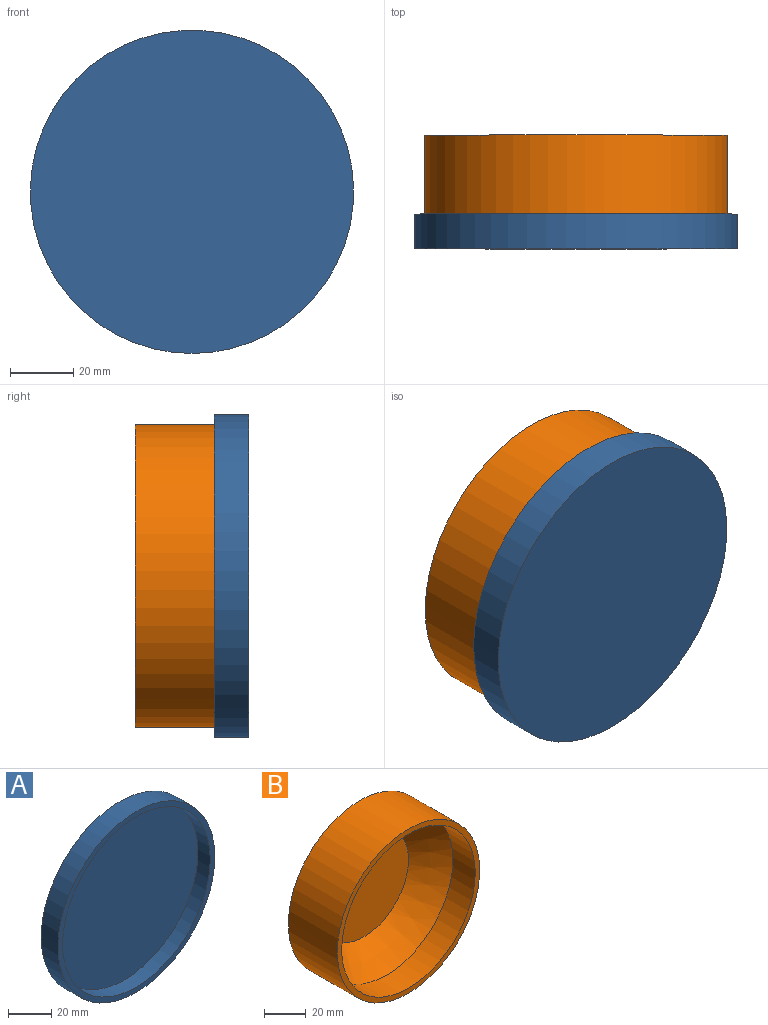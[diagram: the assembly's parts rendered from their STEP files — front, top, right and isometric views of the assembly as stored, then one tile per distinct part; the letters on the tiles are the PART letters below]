
ASSEMBLY  parts=2 mates=1
PART A: 5 faces, bbox 102.5x11x102.5 mm
  f0: cylinder r=48.25mm len=96.5mm, axis (0,1,0), area 2425.3mm2, adj f2,f3
  f1: cylinder r=51.25mm len=102.5mm, axis (0,1,0), area 3542.1mm2, adj f2,f4
  f2: plane 102.5x102.5mm, normal (0,-1,0), area 937.8mm2, adj f0,f1
  f3: plane 96.5x96.5mm, normal (0,-1,0), area 7313.8mm2, adj f0
  f4: plane 102.5x102.5mm, normal (0,1,0), area 8251.6mm2, adj f1
PART B: 6 faces, bbox 96x33x96 mm
  f0: cylinder r=45mm len=90mm, axis (0,1,0), area 4241.2mm2, adj f2,f5
  f1: cylinder r=48mm len=96mm, axis (0,1,0), area 9952.6mm2, adj f2,f4
  f2: plane 96x96mm, normal (0,-1,0), area 876.5mm2, adj f0,f1
  f3: plane 60x60mm, normal (0,-1,0), area 2827.4mm2, adj f5
  f4: plane 96x96mm, normal (0,1,0), area 7238.2mm2, adj f1
  f5: cone r=30mm half-angle=45deg, axis (0,-1,0), area 4998.2mm2, adj f0,f3
PLACE A rot(axis=(0,0,-1),180deg) t=(-82.93,-9.71,-38.66)mm
PLACE B t=(-82.93,20.29,-38.66)mm
MATE revolute B.f0 <-> A.f0  axis (0,-1,0) through (-82.93,-9.71,-38.66)mm
